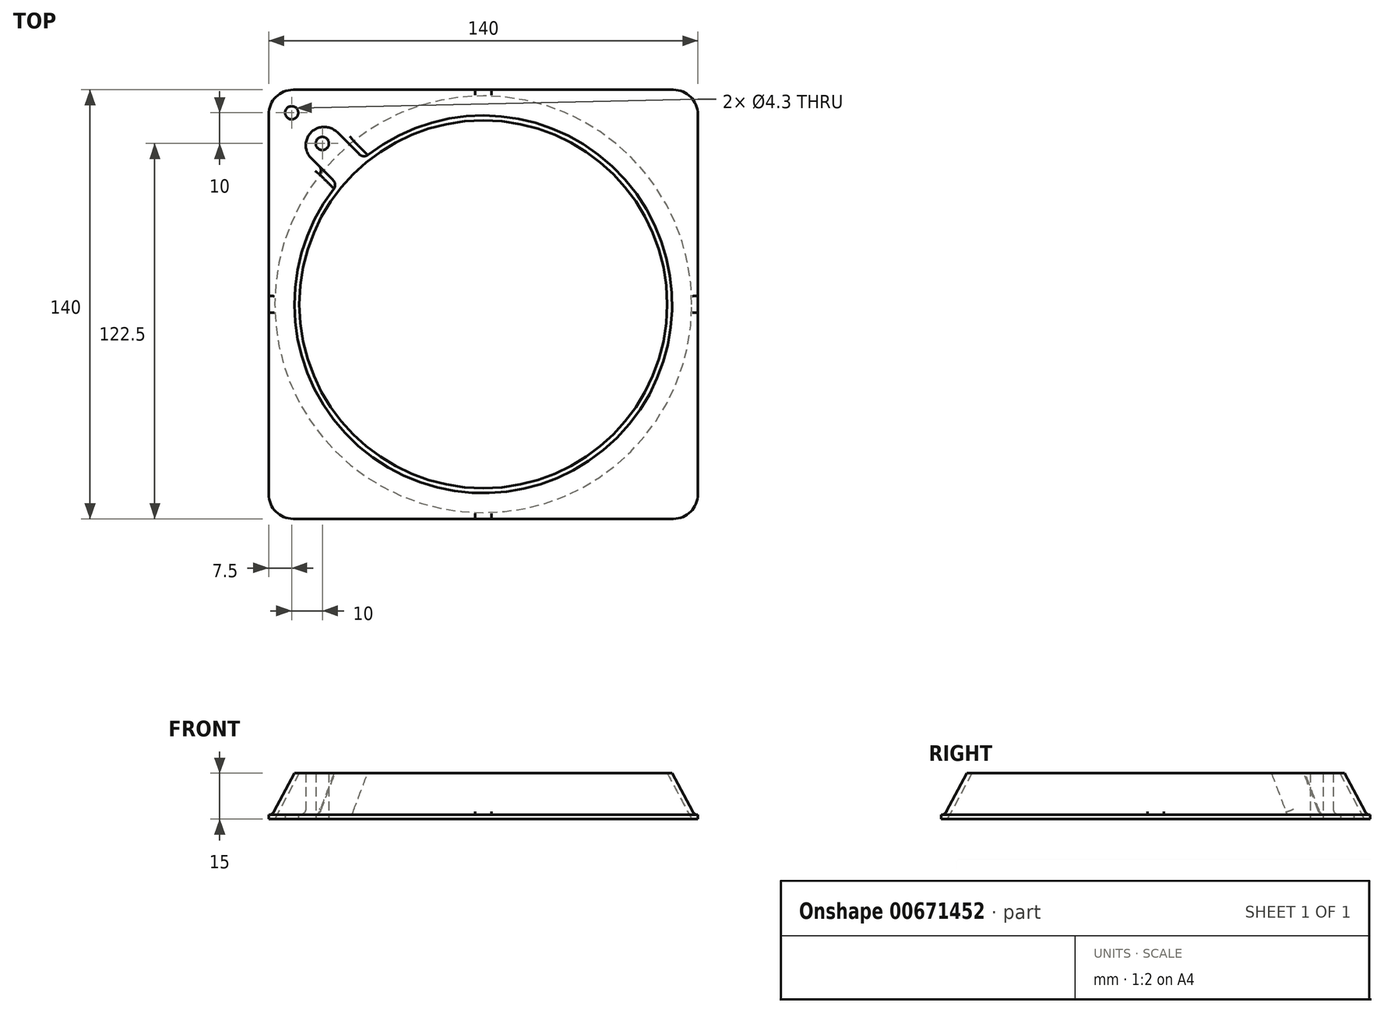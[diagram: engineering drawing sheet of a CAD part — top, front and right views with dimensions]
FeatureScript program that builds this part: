
annotation { "Feature Type Name" : "Feature", "Feature Type Description" : "" }
export const myFeature = defineFeature(function(context is Context, id is Id, definition is map)
    precondition{}
    {
        {
            var Q0;
            Q0=qCreatedBy(makeId("Top.planeOp"),FACE);
            var sketch = newSketch(context, id + "F0", { "sketchPlane" : qUnion([Q0])});
            skLineSegment(sketch, "E0.bottom", {"start": v(-70, 70) * mm, "end": v(70, 70) * mm});
            skLineSegment(sketch, "E0.top", {"start": v(-70, -70) * mm, "end": v(70, -70) * mm});
            skLineSegment(sketch, "E0.left", {"start": v(-70, 70) * mm, "end": v(-70, -70) * mm});
            skLineSegment(sketch, "E0.right", {"start": v(70, 70) * mm, "end": v(70, -70) * mm});
            skSolve(sketch);
        }
        {
            var Q0;
            Q0=qSketchRegion(id+"F0",true);
            extrude(context, id + "F1", {"entities" : qUnion([Q0]), "depth" : 15 * mm, "offsetDistance" : 25 * mm});
        }
        {
            var Q0;
            Q0=qCreatedBy(makeId("Top.planeOp"),FACE);
            var sketch = newSketch(context, id + "F2", { "sketchPlane" : qUnion([Q0])});
            skCircle(sketch, "E1", {"center": v(-62.5, 62.5) * mm, "radius": 2.15 * mm});
            skSolve(sketch);
        }
        {
            var Q0;
            Q0=qCreatedBy(makeId("Right.planeOp"),FACE);
            var sketch = newSketch(context, id + "F3", { "sketchPlane" : qUnion([Q0])});
            skLineSegment(sketch, "E2", {"start": v(0, -23.45) * mm, "end": v(0, 54.65) * mm, "construction": true});
            skSolve(sketch);
        }
        {
            var Q0;
            Q0=qCreatedBy(makeId("Top.planeOp"),FACE);
            var sketch = newSketch(context, id + "F4", { "sketchPlane" : qUnion([Q0])});
            skCircle(sketch, "E3", {"center": v(0, 0) * mm, "radius": 68 * mm});
            skSolve(sketch);
        }
        {
            var Q0;
            Q0=makeQuery(id+"F0.imprint","IMPRINT",FACE,{"disambiguationData":[TD([[makeQuery(id+"F0.imprint","IMPRINT",EDGE,{"derivedFrom":sQuery(id+"F0.wireOp",EDGE,"E0.bottom")}),-1.0]])]});
            var sketch = newSketch(context, id + "F5", { "sketchPlane" : qUnion([Q0])});
            skCircle(sketch, "E4", {"center": v(0, 0) * mm, "radius": 69.6 * mm});
            skLineSegment(sketch, "E5.bottom", {"start": v(-83.67, 77.05) * mm, "end": v(82.18, 77.05) * mm});
            skLineSegment(sketch, "E5.top", {"start": v(-83.67, -76.06) * mm, "end": v(82.18, -76.06) * mm});
            skLineSegment(sketch, "E5.left", {"start": v(-83.67, 77.05) * mm, "end": v(-83.67, -76.06) * mm});
            skLineSegment(sketch, "E5.right", {"start": v(82.18, 77.05) * mm, "end": v(82.18, -76.06) * mm});
            skSolve(sketch);
        }
        {
            var Q0;
            Q0=qSketchRegion(id+"F5",true);
            extrude(context, id + "F6", {"entities" : qUnion([Q0]), "operationType" : NewBodyOperationType.REMOVE, "depth" : 15 * mm, "offsetDistance" : 25 * mm, "hasDraft" : true, "draftAngle" : 28.07 * degree, "hasSecondDirection" : true, "secondDirectionOppositeDirection" : false, "secondDirectionDepth" : 1.4 * mm});
        }
        {
            var Q0;
            Q0=qCreatedBy(makeId("Top.planeOp"),FACE);
            var sketch = newSketch(context, id + "F7", { "sketchPlane" : qUnion([Q0])});
            skCircle(sketch, "E6", {"center": v(-52.5, 52.5) * mm, "radius": 2.15 * mm});
            skSolve(sketch);
        }
        {
            var Q0;
            Q0=makeQuery(id+"F0.imprint","IMPRINT",FACE,{"disambiguationData":[TD([[makeQuery(id+"F0.imprint","IMPRINT",EDGE,{"derivedFrom":sQuery(id+"F0.wireOp",EDGE,"E0.bottom")}),-1.0]])]});
            var sketch = newSketch(context, id + "F8", { "sketchPlane" : qUnion([Q0])});
            skLineSegment(sketch, "E7", {"start": v(-45.5, 37.02) * mm, "end": v(-37.02, 45.5) * mm});
            skLineSegment(sketch, "E8", {"start": v(0, 0) * mm, "end": v(-70, 70) * mm, "construction": true});
            skLineSegment(sketch, "E9", {"start": v(-45.5, 37.02) * mm, "end": v(-60.38, 51.9) * mm});
            skLineSegment(sketch, "E10", {"start": v(-37.02, 45.5) * mm, "end": v(-51.9, 60.38) * mm});
            skLineSegment(sketch, "E11", {"start": v(-60.38, 51.9) * mm, "end": v(-51.9, 60.38) * mm});
            skSolve(sketch);
        }
        {
            var Q0;
            Q0=qSketchRegion(id+"F8",true);
            extrude(context, id + "F9", {"entities" : qUnion([Q0]), "operationType" : NewBodyOperationType.ADD, "depth" : 15 * mm, "offsetDistance" : 25 * mm});
        }
        {
            var Q0;
            Q0=qSketchRegion(id+"F2",true);
            extrude(context, id + "F10", {"entities" : qUnion([Q0]), "operationType" : NewBodyOperationType.REMOVE, "depth" : 5 * mm, "offsetDistance" : 25 * mm});
        }
        {
            var Q0;
            Q0=qSketchRegion(id+"F4",true);
            extrude(context, id + "F11", {"entities" : qUnion([Q0]), "operationType" : NewBodyOperationType.REMOVE, "depth" : 15 * mm, "offsetDistance" : 25 * mm, "hasDraft" : true, "draftAngle" : 28.07 * degree, "draftPullDirection" : true});
        }
        {
            var Q0;
            Q0=makeQuery(id+"F9.boolean.opBoolean","MERGE",EDGE,{"derivedFrom":[makeQuery(id+"F1.opExtrude","SWEPT_EDGE",EDGE,{"disambiguationData":[OSD([sQuery(id+"F0.wireOp",EDGE,"E0.bottom"),sQuery(id+"F0.wireOp",EDGE,"E0.left")])]}),makeQuery(id+"F9.opExtrude","SWEPT_EDGE",EDGE,{"disambiguationData":[OSD([sQuery(id+"F8.wireOp",EDGE,"bcqxiliO-g36q-Js58-HRms-isVHzeuhr4qR"),sQuery(id+"F8.wireOp",EDGE,"sepJio0f-Bdl7-0CLp-PTzf-5zJ3YjW6fdva")])]})]});
            var Q1;
            Q1=makeQuery(id+"FmQ22TMhTTGu5hA_1.3.F9.boolean.opBoolean","MERGE",EDGE,{"derivedFrom":[makeQuery(id+"F1.opExtrude","SWEPT_EDGE",EDGE,{"disambiguationData":[OSD([sQuery(id+"F0.wireOp",EDGE,"E0.bottom"),sQuery(id+"F0.wireOp",EDGE,"E0.right")])]}),makeQuery(id+"FmQ22TMhTTGu5hA_1.3.F9.opExtrude","SWEPT_EDGE",EDGE,{"disambiguationData":[OSD([sQuery(id+"F8.wireOp",EDGE,"bcqxiliO-g36q-Js58-HRms-isVHzeuhr4qR"),sQuery(id+"F8.wireOp",EDGE,"sepJio0f-Bdl7-0CLp-PTzf-5zJ3YjW6fdva")])]})]});
            var Q2;
            Q2=makeQuery(id+"FmQ22TMhTTGu5hA_1.2.F9.boolean.opBoolean","MERGE",EDGE,{"derivedFrom":[makeQuery(id+"F1.opExtrude","SWEPT_EDGE",EDGE,{"disambiguationData":[OSD([sQuery(id+"F0.wireOp",EDGE,"E0.top"),sQuery(id+"F0.wireOp",EDGE,"E0.right")])]}),makeQuery(id+"FmQ22TMhTTGu5hA_1.2.F9.opExtrude","SWEPT_EDGE",EDGE,{"disambiguationData":[OSD([sQuery(id+"F8.wireOp",EDGE,"bcqxiliO-g36q-Js58-HRms-isVHzeuhr4qR"),sQuery(id+"F8.wireOp",EDGE,"sepJio0f-Bdl7-0CLp-PTzf-5zJ3YjW6fdva")])]})]});
            var Q3;
            Q3=makeQuery(id+"FmQ22TMhTTGu5hA_1.1.F9.boolean.opBoolean","MERGE",EDGE,{"derivedFrom":[makeQuery(id+"F1.opExtrude","SWEPT_EDGE",EDGE,{"disambiguationData":[OSD([sQuery(id+"F0.wireOp",EDGE,"E0.top"),sQuery(id+"F0.wireOp",EDGE,"E0.left")])]}),makeQuery(id+"FmQ22TMhTTGu5hA_1.1.F9.opExtrude","SWEPT_EDGE",EDGE,{"disambiguationData":[OSD([sQuery(id+"F8.wireOp",EDGE,"bcqxiliO-g36q-Js58-HRms-isVHzeuhr4qR"),sQuery(id+"F8.wireOp",EDGE,"sepJio0f-Bdl7-0CLp-PTzf-5zJ3YjW6fdva")])]})]});
            fillet(context, id + "F12", {"entities" : qUnion([Q0, Q1, Q2, Q3]), "radius" : 8 * mm, "tangentPropagation" : true, "allowEdgeOverflow" : false});
        }
        {
            var Q0;
            Q0=qSketchRegion(id+"F7",true);
            extrude(context, id + "F13", {"entities" : qUnion([Q0]), "operationType" : NewBodyOperationType.REMOVE, "depth" : 30 * mm, "offsetDistance" : 25 * mm});
        }
        {
            var Q0;
            Q0=makeQuery(id+"F9.opExtrude","SWEPT_EDGE",EDGE,{"disambiguationData":[OSD([sQuery(id+"F8.wireOp",EDGE,"E9"),sQuery(id+"F8.wireOp",EDGE,"E11")])]});
            var Q1;
            Q1=makeQuery(id+"F9.opExtrude","SWEPT_EDGE",EDGE,{"disambiguationData":[OSD([sQuery(id+"F8.wireOp",EDGE,"E10"),sQuery(id+"F8.wireOp",EDGE,"E11")])]});
            var Q2;
            Q2=makeQuery(id+"FmQ22TMhTTGu5hA_1.1.F9.opExtrude","SWEPT_EDGE",EDGE,{"disambiguationData":[OSD([sQuery(id+"F8.wireOp",EDGE,"E10"),sQuery(id+"F8.wireOp",EDGE,"E11")])]});
            var Q3;
            Q3=makeQuery(id+"FmQ22TMhTTGu5hA_1.1.F9.opExtrude","SWEPT_EDGE",EDGE,{"disambiguationData":[OSD([sQuery(id+"F8.wireOp",EDGE,"E9"),sQuery(id+"F8.wireOp",EDGE,"E11")])]});
            var Q4;
            Q4=makeQuery(id+"FmQ22TMhTTGu5hA_1.2.F9.opExtrude","SWEPT_EDGE",EDGE,{"disambiguationData":[OSD([sQuery(id+"F8.wireOp",EDGE,"E10"),sQuery(id+"F8.wireOp",EDGE,"E11")])]});
            var Q5;
            Q5=makeQuery(id+"FmQ22TMhTTGu5hA_1.2.F9.opExtrude","SWEPT_EDGE",EDGE,{"disambiguationData":[OSD([sQuery(id+"F8.wireOp",EDGE,"E9"),sQuery(id+"F8.wireOp",EDGE,"E11")])]});
            var Q6;
            Q6=makeQuery(id+"FmQ22TMhTTGu5hA_1.3.F9.opExtrude","SWEPT_EDGE",EDGE,{"disambiguationData":[OSD([sQuery(id+"F8.wireOp",EDGE,"E10"),sQuery(id+"F8.wireOp",EDGE,"E11")])]});
            var Q7;
            Q7=makeQuery(id+"FmQ22TMhTTGu5hA_1.3.F9.opExtrude","SWEPT_EDGE",EDGE,{"disambiguationData":[OSD([sQuery(id+"F8.wireOp",EDGE,"E9"),sQuery(id+"F8.wireOp",EDGE,"E11")])]});
            fillet(context, id + "F14", {"entities" : qUnion([Q0, Q1, Q2, Q3, Q4, Q5, Q6, Q7]), "radius" : 6 * mm, "tangentPropagation" : true, "allowEdgeOverflow" : false});
        }
        {
            var Q0;
            {var subQ0=sQuery(id+"F5.wireOp",EDGE,"E4");var subQ2=sQuery(id+"F8.wireOp",EDGE,"E10");var subQ4=makeQuery(id+"FmQ22TMhTTGu5hA_1.1.F9.opExtrude","SWEPT_FACE",FACE,{"disambiguationData":[OSD([sQuery(id+"F8.wireOp",EDGE,"E9")])]});Q0=makeQuery(id+"FmQ22TMhTTGu5hA_1.2.F9.boolean.opBoolean","SPLIT",EDGE,{"disambiguationData":[TD([subQ4])],"derivedFrom":makeQuery(id+"FmQ22TMhTTGu5hA_1.1.F9.boolean.opBoolean","SPLIT",EDGE,{"disambiguationData":[TD([makeQuery(id+"F9.opExtrude","SWEPT_FACE",FACE,{"disambiguationData":[OSD([subQ2])]})])],"derivedFrom":makeQuery(id+"F6.boolean.opBoolean","COPY",EDGE,{"derivedFrom":makeQuery(id+"F6.opExtrude","CAP_EDGE",EDGE,{"disambiguationData":[OSD([subQ0])],"isStart":true})})})});}
            var Q1;
            {var subQ0=sQuery(id+"F5.wireOp",EDGE,"E4");Q1=makeQuery(id+"FmQ22TMhTTGu5hA_1.1.F9.boolean.opBoolean","SPLIT",EDGE,{"disambiguationData":[TD([makeQuery(id+"F9.opExtrude","SWEPT_FACE",FACE,{"disambiguationData":[OSD([sQuery(id+"F8.wireOp",EDGE,"E9")])]})])],"derivedFrom":makeQuery(id+"F6.boolean.opBoolean","COPY",EDGE,{"derivedFrom":makeQuery(id+"F6.opExtrude","CAP_EDGE",EDGE,{"disambiguationData":[OSD([subQ0])],"isStart":true})})});}
            var Q2;
            {var subQ0=sQuery(id+"F5.wireOp",EDGE,"E4");var subQ3=sQuery(id+"F8.wireOp",EDGE,"E9");var subQ4=makeQuery(id+"FmQ22TMhTTGu5hA_1.2.F9.opExtrude","SWEPT_FACE",FACE,{"disambiguationData":[OSD([subQ3])]});var subQ5=sQuery(id+"F8.wireOp",EDGE,"E10");var subQ6=makeQuery(id+"F9.opExtrude","SWEPT_FACE",FACE,{"disambiguationData":[OSD([subQ5])]});Q2=makeQuery(id+"FmQ22TMhTTGu5hA_1.3.F9.boolean.opBoolean","SPLIT",EDGE,{"disambiguationData":[TD([subQ4])],"derivedFrom":makeQuery(id+"FmQ22TMhTTGu5hA_1.2.F9.boolean.opBoolean","SPLIT",EDGE,{"disambiguationData":[TD([subQ6])],"derivedFrom":makeQuery(id+"FmQ22TMhTTGu5hA_1.1.F9.boolean.opBoolean","SPLIT",EDGE,{"disambiguationData":[TD([subQ6])],"derivedFrom":makeQuery(id+"F6.boolean.opBoolean","COPY",EDGE,{"derivedFrom":makeQuery(id+"F6.opExtrude","CAP_EDGE",EDGE,{"disambiguationData":[OSD([subQ0])],"isStart":true})})})})});}
            var Q3;
            {var subQ0=sQuery(id+"F5.wireOp",EDGE,"E4");var subQ4=makeQuery(id+"F9.opExtrude","SWEPT_FACE",FACE,{"disambiguationData":[OSD([sQuery(id+"F8.wireOp",EDGE,"E10")])]});Q3=makeQuery(id+"FmQ22TMhTTGu5hA_1.3.F9.boolean.opBoolean","SPLIT",EDGE,{"disambiguationData":[TD([subQ4])],"derivedFrom":makeQuery(id+"FmQ22TMhTTGu5hA_1.2.F9.boolean.opBoolean","SPLIT",EDGE,{"disambiguationData":[TD([subQ4])],"derivedFrom":makeQuery(id+"FmQ22TMhTTGu5hA_1.1.F9.boolean.opBoolean","SPLIT",EDGE,{"disambiguationData":[TD([subQ4])],"derivedFrom":makeQuery(id+"F6.boolean.opBoolean","COPY",EDGE,{"derivedFrom":makeQuery(id+"F6.opExtrude","CAP_EDGE",EDGE,{"disambiguationData":[OSD([subQ0])],"isStart":true})})})})});}
            var Q4;
            Q4=makeQuery(id+"FmQ22TMhTTGu5hA_1.1.F9.boolean.opBoolean","INTERSECT",EDGE,{"derivedFrom":[makeQuery(id+"F6.boolean.opBoolean","COPY",FACE,{"derivedFrom":makeQuery(id+"F6.opExtrude","SWEPT_FACE",FACE,{"disambiguationData":[OSD([sQuery(id+"F5.wireOp",EDGE,"E4")])]})}),makeQuery(id+"FmQ22TMhTTGu5hA_1.1.F9.opExtrude","SWEPT_FACE",FACE,{"disambiguationData":[OSD([sQuery(id+"F8.wireOp",EDGE,"E9")])]})]});
            var Q5;
            {var subQ0=sQuery(id+"F8.wireOp",EDGE,"E10");var subQ4=sQuery(id+"F5.wireOp",EDGE,"E4");Q5=makeQuery(id+"FmQ22TMhTTGu5hA_1.2.F9.boolean.opBoolean","INTERSECT",EDGE,{"derivedFrom":[makeQuery(id+"FmQ22TMhTTGu5hA_1.1.F9.boolean.opBoolean","SPLIT",FACE,{"disambiguationData":[TD([makeQuery(id+"F9.opExtrude","SWEPT_FACE",FACE,{"disambiguationData":[OSD([subQ0])]})])],"derivedFrom":makeQuery(id+"F6.boolean.opBoolean","COPY",FACE,{"derivedFrom":makeQuery(id+"F6.opExtrude","SWEPT_FACE",FACE,{"disambiguationData":[OSD([subQ4])]})})}),makeQuery(id+"FmQ22TMhTTGu5hA_1.2.F9.opExtrude","SWEPT_FACE",FACE,{"disambiguationData":[OSD([subQ0])]})]});}
            var Q6;
            Q6=makeQuery(id+"F14.opFillet","BLEND_EDGE",EDGE,{"blendedFrom":[makeQuery(id+"FmQ22TMhTTGu5hA_1.1.F9.opExtrude","SWEPT_EDGE",EDGE,{"disambiguationData":[OSD([sQuery(id+"F8.wireOp",EDGE,"E9"),sQuery(id+"F8.wireOp",EDGE,"E11")])]}),makeQuery(id+"F6.boolean.opBoolean","COPY",FACE,{"derivedFrom":makeQuery(id+"F6.opExtrude","CAP_FACE",FACE,{"disambiguationData":[OSD([sQuery(id+"F5.wireOp",EDGE,"E4"),sQuery(id+"F5.wireOp",EDGE,"E5.bottom"),sQuery(id+"F5.wireOp",EDGE,"E5.top"),sQuery(id+"F5.wireOp",EDGE,"E5.left"),sQuery(id+"F5.wireOp",EDGE,"E5.right")])],"isStart":true})})],"blendedInto":[makeQuery(id+"F6.boolean.opBoolean","COPY",FACE,{"derivedFrom":makeQuery(id+"F6.opExtrude","CAP_FACE",FACE,{"disambiguationData":[OSD([sQuery(id+"F5.wireOp",EDGE,"E4"),sQuery(id+"F5.wireOp",EDGE,"E5.bottom"),sQuery(id+"F5.wireOp",EDGE,"E5.top"),sQuery(id+"F5.wireOp",EDGE,"E5.left"),sQuery(id+"F5.wireOp",EDGE,"E5.right")])],"isStart":true})})]});
            var Q7;
            Q7=makeQuery(id+"FmQ22TMhTTGu5hA_1.1.F9.boolean.opBoolean","INTERSECT",EDGE,{"derivedFrom":[makeQuery(id+"F6.boolean.opBoolean","COPY",FACE,{"derivedFrom":makeQuery(id+"F6.opExtrude","SWEPT_FACE",FACE,{"disambiguationData":[OSD([sQuery(id+"F5.wireOp",EDGE,"E4")])]})}),makeQuery(id+"FmQ22TMhTTGu5hA_1.1.F9.opExtrude","SWEPT_FACE",FACE,{"disambiguationData":[OSD([sQuery(id+"F8.wireOp",EDGE,"E10")])]})]});
            var Q8;
            Q8=makeQuery(id+"F9.boolean.opBoolean","INTERSECT",EDGE,{"derivedFrom":[makeQuery(id+"F6.boolean.opBoolean","COPY",FACE,{"derivedFrom":makeQuery(id+"F6.opExtrude","SWEPT_FACE",FACE,{"disambiguationData":[OSD([sQuery(id+"F5.wireOp",EDGE,"E4")])]})}),makeQuery(id+"F9.opExtrude","SWEPT_FACE",FACE,{"disambiguationData":[OSD([sQuery(id+"F8.wireOp",EDGE,"E9")])]})]});
            var Q9;
            Q9=makeQuery(id+"F14.opFillet","BLEND_EDGE",EDGE,{"blendedFrom":[makeQuery(id+"F9.opExtrude","SWEPT_EDGE",EDGE,{"disambiguationData":[OSD([sQuery(id+"F8.wireOp",EDGE,"E9"),sQuery(id+"F8.wireOp",EDGE,"E11")])]}),makeQuery(id+"F6.boolean.opBoolean","COPY",FACE,{"derivedFrom":makeQuery(id+"F6.opExtrude","CAP_FACE",FACE,{"disambiguationData":[OSD([sQuery(id+"F5.wireOp",EDGE,"E4"),sQuery(id+"F5.wireOp",EDGE,"E5.bottom"),sQuery(id+"F5.wireOp",EDGE,"E5.top"),sQuery(id+"F5.wireOp",EDGE,"E5.left"),sQuery(id+"F5.wireOp",EDGE,"E5.right")])],"isStart":true})})],"blendedInto":[makeQuery(id+"F6.boolean.opBoolean","COPY",FACE,{"derivedFrom":makeQuery(id+"F6.opExtrude","CAP_FACE",FACE,{"disambiguationData":[OSD([sQuery(id+"F5.wireOp",EDGE,"E4"),sQuery(id+"F5.wireOp",EDGE,"E5.bottom"),sQuery(id+"F5.wireOp",EDGE,"E5.top"),sQuery(id+"F5.wireOp",EDGE,"E5.left"),sQuery(id+"F5.wireOp",EDGE,"E5.right")])],"isStart":true})})]});
            var Q10;
            Q10=makeQuery(id+"F14.opFillet","BLEND_EDGE",EDGE,{"blendedFrom":[makeQuery(id+"FmQ22TMhTTGu5hA_1.2.F9.opExtrude","SWEPT_EDGE",EDGE,{"disambiguationData":[OSD([sQuery(id+"F8.wireOp",EDGE,"E9"),sQuery(id+"F8.wireOp",EDGE,"E11")])]}),makeQuery(id+"F6.boolean.opBoolean","COPY",FACE,{"derivedFrom":makeQuery(id+"F6.opExtrude","CAP_FACE",FACE,{"disambiguationData":[OSD([sQuery(id+"F5.wireOp",EDGE,"E4"),sQuery(id+"F5.wireOp",EDGE,"E5.bottom"),sQuery(id+"F5.wireOp",EDGE,"E5.top"),sQuery(id+"F5.wireOp",EDGE,"E5.left"),sQuery(id+"F5.wireOp",EDGE,"E5.right")])],"isStart":true})})],"blendedInto":[makeQuery(id+"F6.boolean.opBoolean","COPY",FACE,{"derivedFrom":makeQuery(id+"F6.opExtrude","CAP_FACE",FACE,{"disambiguationData":[OSD([sQuery(id+"F5.wireOp",EDGE,"E4"),sQuery(id+"F5.wireOp",EDGE,"E5.bottom"),sQuery(id+"F5.wireOp",EDGE,"E5.top"),sQuery(id+"F5.wireOp",EDGE,"E5.left"),sQuery(id+"F5.wireOp",EDGE,"E5.right")])],"isStart":true})})]});
            var Q11;
            Q11=makeQuery(id+"F14.opFillet","BLEND_EDGE",EDGE,{"blendedFrom":[makeQuery(id+"FmQ22TMhTTGu5hA_1.3.F9.opExtrude","SWEPT_EDGE",EDGE,{"disambiguationData":[OSD([sQuery(id+"F8.wireOp",EDGE,"E9"),sQuery(id+"F8.wireOp",EDGE,"E11")])]}),makeQuery(id+"F6.boolean.opBoolean","COPY",FACE,{"derivedFrom":makeQuery(id+"F6.opExtrude","CAP_FACE",FACE,{"disambiguationData":[OSD([sQuery(id+"F5.wireOp",EDGE,"E4"),sQuery(id+"F5.wireOp",EDGE,"E5.bottom"),sQuery(id+"F5.wireOp",EDGE,"E5.top"),sQuery(id+"F5.wireOp",EDGE,"E5.left"),sQuery(id+"F5.wireOp",EDGE,"E5.right")])],"isStart":true})})],"blendedInto":[makeQuery(id+"F6.boolean.opBoolean","COPY",FACE,{"derivedFrom":makeQuery(id+"F6.opExtrude","CAP_FACE",FACE,{"disambiguationData":[OSD([sQuery(id+"F5.wireOp",EDGE,"E4"),sQuery(id+"F5.wireOp",EDGE,"E5.bottom"),sQuery(id+"F5.wireOp",EDGE,"E5.top"),sQuery(id+"F5.wireOp",EDGE,"E5.left"),sQuery(id+"F5.wireOp",EDGE,"E5.right")])],"isStart":true})})]});
            var Q12;
            {var subQ0=sQuery(id+"F8.wireOp",EDGE,"E10");var subQ1=makeQuery(id+"F9.opExtrude","SWEPT_FACE",FACE,{"disambiguationData":[OSD([subQ0])]});var subQ6=sQuery(id+"F5.wireOp",EDGE,"E4");Q12=makeQuery(id+"FmQ22TMhTTGu5hA_1.3.F9.boolean.opBoolean","INTERSECT",EDGE,{"derivedFrom":[makeQuery(id+"FmQ22TMhTTGu5hA_1.2.F9.boolean.opBoolean","SPLIT",FACE,{"disambiguationData":[TD([subQ1])],"derivedFrom":makeQuery(id+"FmQ22TMhTTGu5hA_1.1.F9.boolean.opBoolean","SPLIT",FACE,{"disambiguationData":[TD([subQ1])],"derivedFrom":makeQuery(id+"F6.boolean.opBoolean","COPY",FACE,{"derivedFrom":makeQuery(id+"F6.opExtrude","SWEPT_FACE",FACE,{"disambiguationData":[OSD([subQ6])]})})})}),makeQuery(id+"FmQ22TMhTTGu5hA_1.3.F9.opExtrude","SWEPT_FACE",FACE,{"disambiguationData":[OSD([subQ0])]})]});}
            var Q13;
            {var subQ0=sQuery(id+"F8.wireOp",EDGE,"E9");var subQ1=sQuery(id+"F8.wireOp",EDGE,"E10");var subQ2=makeQuery(id+"F9.opExtrude","SWEPT_FACE",FACE,{"disambiguationData":[OSD([subQ1])]});var subQ6=sQuery(id+"F5.wireOp",EDGE,"E4");Q13=makeQuery(id+"FmQ22TMhTTGu5hA_1.3.F9.boolean.opBoolean","INTERSECT",EDGE,{"derivedFrom":[makeQuery(id+"FmQ22TMhTTGu5hA_1.2.F9.boolean.opBoolean","SPLIT",FACE,{"disambiguationData":[TD([subQ2])],"derivedFrom":makeQuery(id+"FmQ22TMhTTGu5hA_1.1.F9.boolean.opBoolean","SPLIT",FACE,{"disambiguationData":[TD([subQ2])],"derivedFrom":makeQuery(id+"F6.boolean.opBoolean","COPY",FACE,{"derivedFrom":makeQuery(id+"F6.opExtrude","SWEPT_FACE",FACE,{"disambiguationData":[OSD([subQ6])]})})})}),makeQuery(id+"FmQ22TMhTTGu5hA_1.3.F9.opExtrude","SWEPT_FACE",FACE,{"disambiguationData":[OSD([subQ0])]})]});}
            var Q14;
            Q14=makeQuery(id+"F9.boolean.opBoolean","INTERSECT",EDGE,{"derivedFrom":[makeQuery(id+"F6.boolean.opBoolean","COPY",FACE,{"derivedFrom":makeQuery(id+"F6.opExtrude","SWEPT_FACE",FACE,{"disambiguationData":[OSD([sQuery(id+"F5.wireOp",EDGE,"E4")])]})}),makeQuery(id+"F9.opExtrude","SWEPT_FACE",FACE,{"disambiguationData":[OSD([sQuery(id+"F8.wireOp",EDGE,"E10")])]})]});
            fillet(context, id + "F15", {"entities" : qUnion([Q0, Q1, Q2, Q3, Q4, Q5, Q6, Q7, Q8, Q9, Q10, Q11, Q12, Q13, Q14]), "radius" : 2 * mm, "tangentPropagation" : true, "allowEdgeOverflow" : false});
        }
    });
